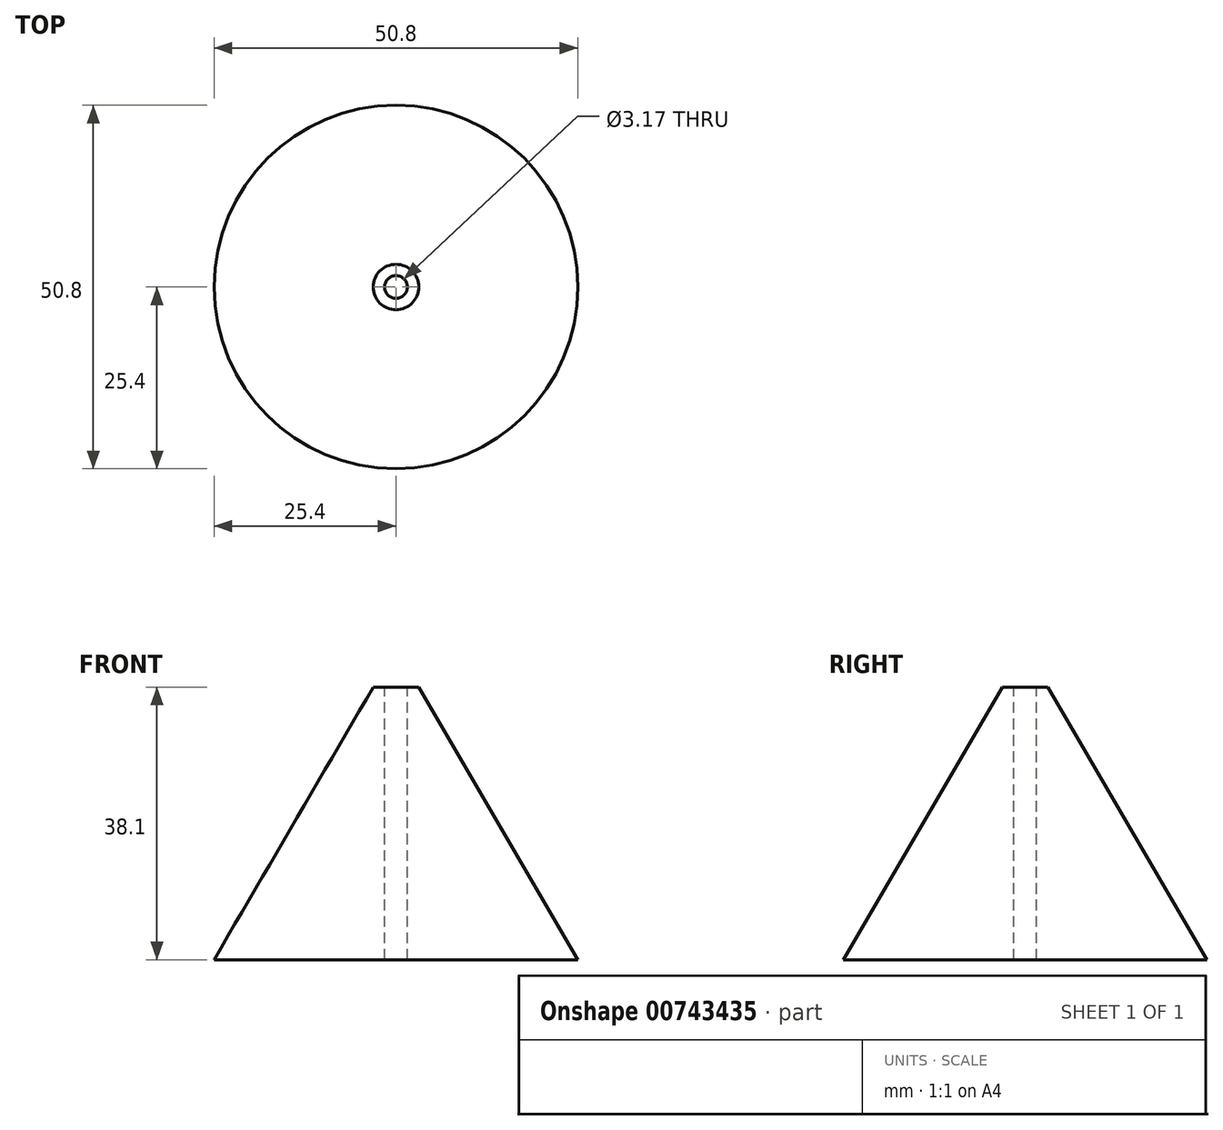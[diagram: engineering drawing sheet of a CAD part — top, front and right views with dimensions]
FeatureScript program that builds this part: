
annotation { "Feature Type Name" : "Feature", "Feature Type Description" : "" }
export const myFeature = defineFeature(function(context is Context, id is Id, definition is map)
    precondition{}
    {
        {
            var Q0;
            Q0=qCreatedBy(makeId("Front.planeOp"),FACE);
            var sketch = newSketch(context, id + "F0", { "sketchPlane" : qUnion([Q0])});
            skLineSegment(sketch, "E0", {"start": v(0, 0) * mm, "end": v(0, 38.1) * mm});
            skLineSegment(sketch, "E1", {"start": v(0, 0) * mm, "end": v(25.4, 0) * mm});
            skLineSegment(sketch, "E2", {"start": v(0, 38.1) * mm, "end": v(3.17, 38.1) * mm});
            skLineSegment(sketch, "E3", {"start": v(3.18, 38.1) * mm, "end": v(25.4, 0) * mm});
            skLineSegment(sketch, "E4", {"start": v(42.29, 46.1) * mm, "end": v(42.29, 8) * mm});
            skLineSegment(sketch, "E5", {"start": v(42.29, 46.1) * mm, "end": v(16.89, 46.1) * mm});
            skLineSegment(sketch, "E6", {"start": v(42.29, 8) * mm, "end": v(39.11, 8) * mm});
            skLineSegment(sketch, "E7", {"start": v(39.11, 8) * mm, "end": v(16.89, 46.1) * mm});
            skLineSegment(sketch, "E8", {"start": v(25.4, 0) * mm, "end": v(39.11, 8) * mm});
            skSolve(sketch);
        }
        {
            var Q0;
            Q0=makeQuery(id+"F0.imprint","IMPRINT",FACE,{"disambiguationData":[TD([[makeQuery(id+"F0.imprint","IMPRINT",EDGE,{"derivedFrom":sQuery(id+"F0.wireOp",EDGE,"E0")}),-1.0]])]});
            var Q1;
            Q1=sQuery(id+"F0.wireOp",EDGE,"E0");
            revolve(context, id + "F1", {"surfaceOperationType" : NewSurfaceOperationType.NEW, "entities" : qUnion([Q0]), "axis" : qUnion([Q1]), "revolveType" : RevolveType.FULL});
        }
        {
            var Q0;
            Q0=makeQuery(id+"F1.opRevolve","SWEPT_FACE",FACE,{"disambiguationData":[OSD([sQuery(id+"F0.wireOp",EDGE,"E2")])]});
            var sketch = newSketch(context, id + "F2", { "sketchPlane" : qUnion([Q0])});
            skCircle(sketch, "E9", {"center": v(0, 0) * mm, "radius": 1.59 * mm});
            skSolve(sketch);
        }
        {
            var Q0;
            Q0=makeQuery(id+"F2.imprint","IMPRINT",FACE,{"disambiguationData":[TD([[makeQuery(id+"F2.imprint","IMPRINT",EDGE,{"derivedFrom":sQuery(id+"F2.wireOp",EDGE,"E9")}),1.0]])]});
            extrude(context, id + "F3", {"entities" : qUnion([Q0]), "operationType" : NewBodyOperationType.REMOVE, "oppositeDirection" : true, "depth" : 38.1 * mm, "offsetDistance" : 25.4 * mm});
        }
    });
